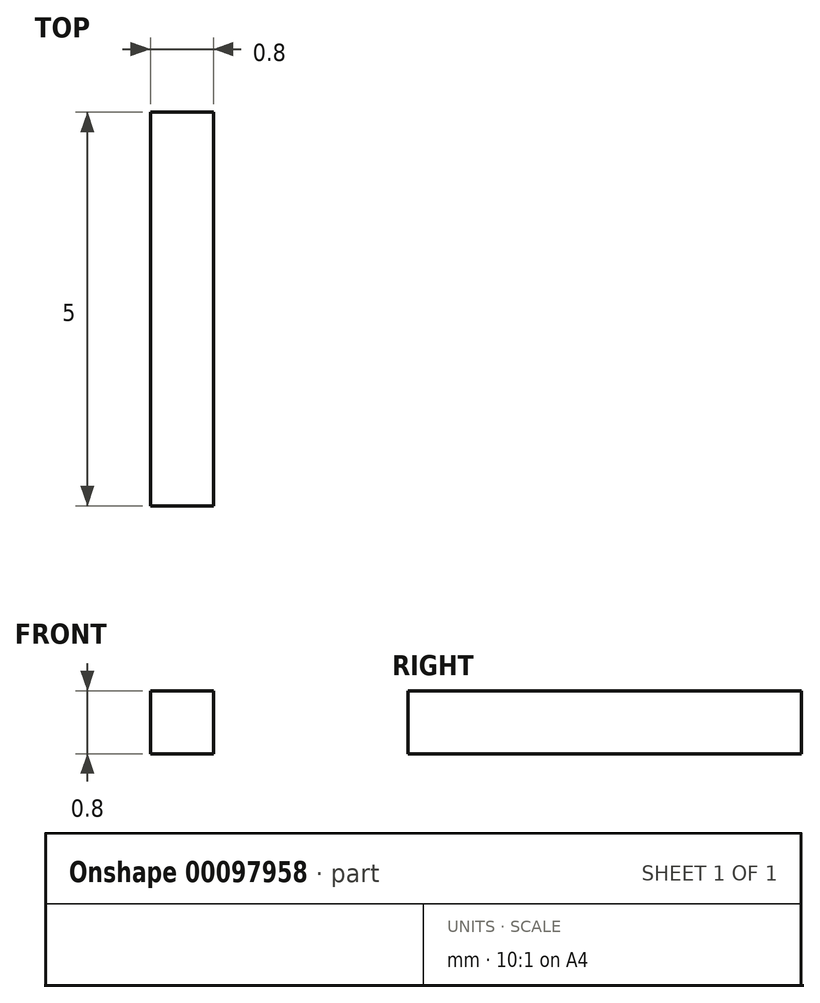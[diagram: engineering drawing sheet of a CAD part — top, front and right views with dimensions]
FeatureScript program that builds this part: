
annotation { "Feature Type Name" : "Feature", "Feature Type Description" : "" }
export const myFeature = defineFeature(function(context is Context, id is Id, definition is map)
    precondition{}
    {
        {
            var Q0;
            Q0=qCreatedBy(makeId("Front.planeOp"),FACE);
            var sketch = newSketch(context, id + "F0", { "sketchPlane" : qUnion([Q0])});
            skLineSegment(sketch, "E0.bottom", {"start": v(0, 0.8) * mm, "end": v(0.8, 0.8) * mm});
            skLineSegment(sketch, "E0.top", {"start": v(0, 0) * mm, "end": v(0.8, 0) * mm});
            skLineSegment(sketch, "E0.left", {"start": v(0, 0.8) * mm, "end": v(0, 0) * mm});
            skLineSegment(sketch, "E0.right", {"start": v(0.8, 0.8) * mm, "end": v(0.8, 0) * mm});
            skSolve(sketch);
        }
        {
            var Q0;
            Q0=makeQuery(id+"F0.imprint","IMPRINT",FACE,{"disambiguationData":[TD([[makeQuery(id+"F0.imprint","IMPRINT",EDGE,{"derivedFrom":sQuery(id+"F0.wireOp",EDGE,"E0.bottom")}),-1.0]])]});
            extrude(context, id + "F1", {"entities" : qUnion([Q0]), "depth" : 5 * mm});
        }
    });
